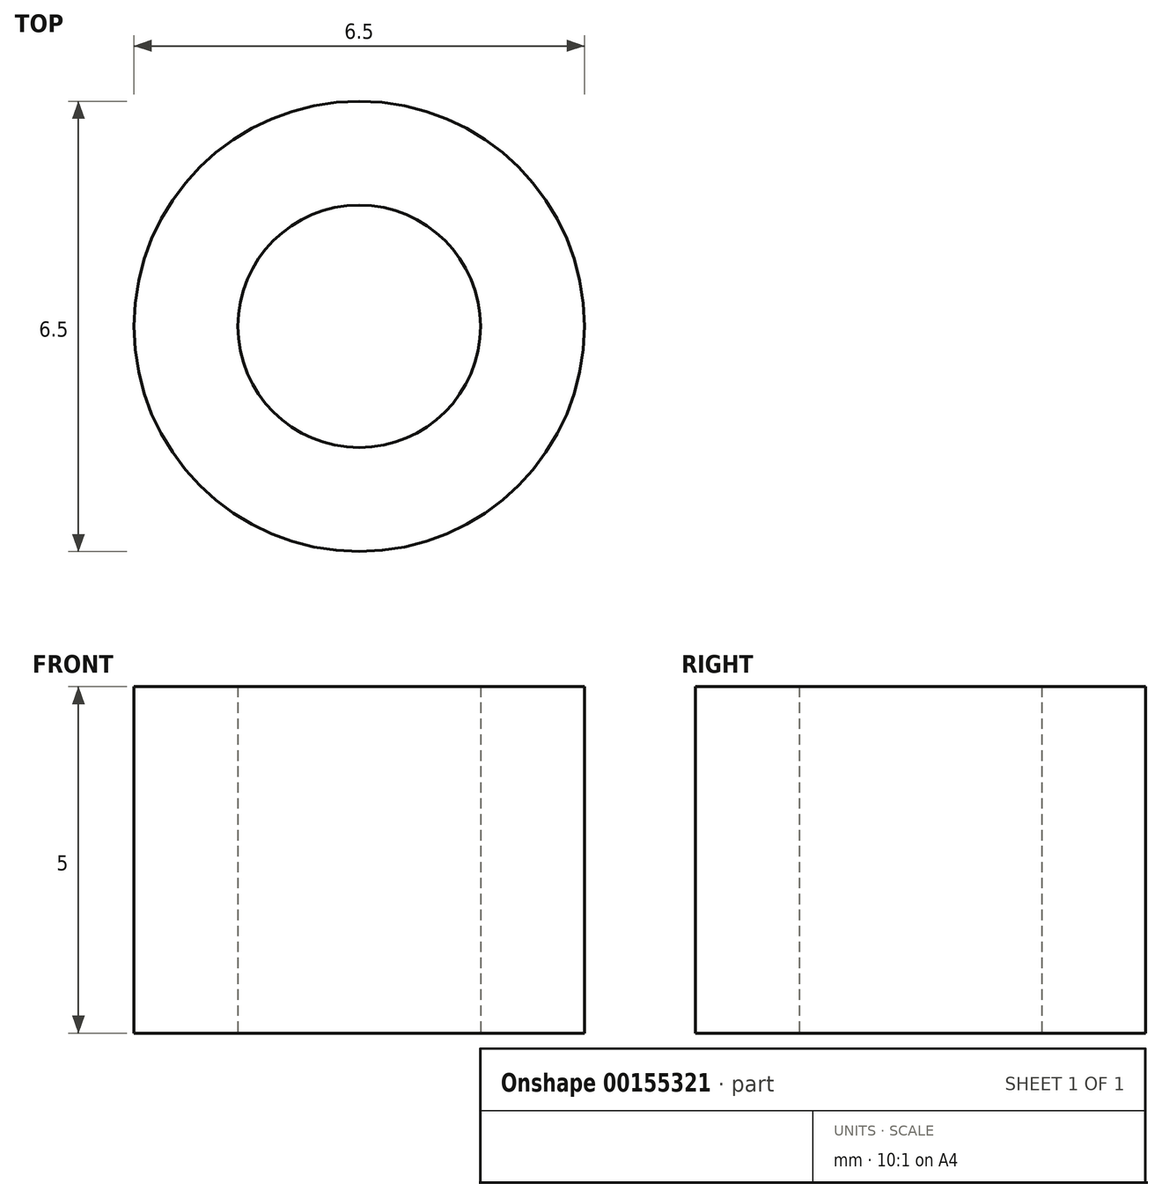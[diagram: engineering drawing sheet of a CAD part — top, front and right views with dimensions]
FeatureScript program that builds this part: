
annotation { "Feature Type Name" : "Feature", "Feature Type Description" : "" }
export const myFeature = defineFeature(function(context is Context, id is Id, definition is map)
    precondition{}
    {
        {
            var Q0;
            Q0=qCreatedBy(makeId("Top.planeOp"),FACE);
            var sketch = newSketch(context, id + "F0", { "sketchPlane" : qUnion([Q0])});
            skCircle(sketch, "E0", {"center": v(0, 0) * mm, "radius": 1.75 * mm});
            skCircle(sketch, "E1", {"center": v(0, 0) * mm, "radius": 3.25 * mm});
            skSolve(sketch);
        }
        {
            var Q0;
            Q0 = qSketchRegion(id + "F0", true);
            extrude(context, id + "F1", {"entities" : qUnion([Q0]), "depth" : 5 * mm});
        }
    });
